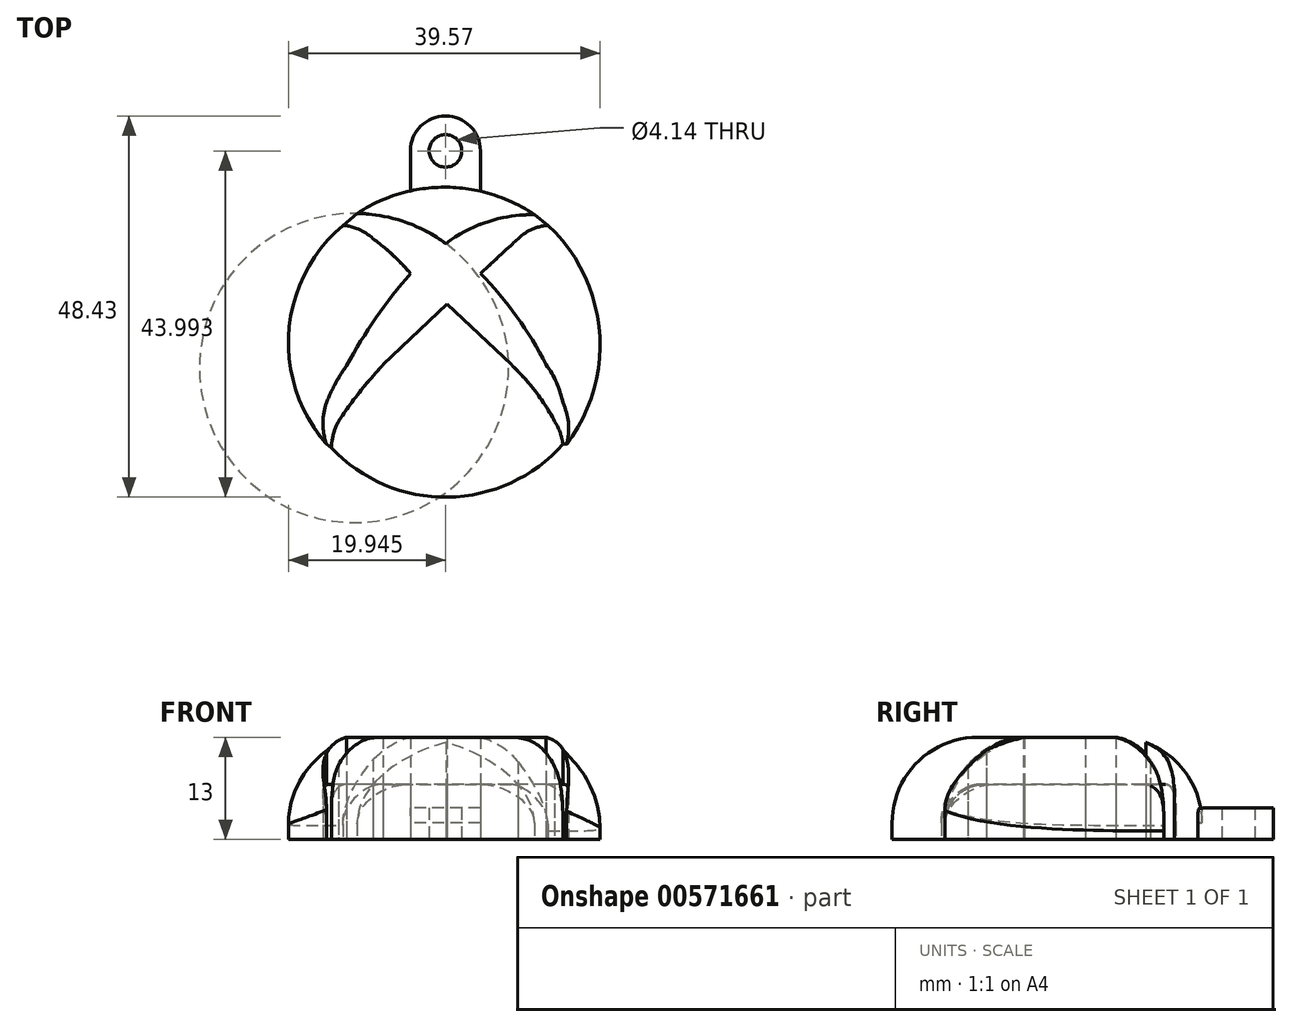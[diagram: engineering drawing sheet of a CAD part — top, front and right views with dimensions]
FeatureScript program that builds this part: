
annotation { "Feature Type Name" : "Feature", "Feature Type Description" : "" }
export const myFeature = defineFeature(function(context is Context, id is Id, definition is map)
    precondition{}
    {
        {
            var Q0;
            Q0=qCreatedBy(makeId("Top.planeOp"),FACE);
            var sketch = newSketch(context, id + "F0", { "sketchPlane" : qUnion([Q0])});
            skArc(sketch, "E0", {"start": v(-15.66, -12.74) * mm, "mid": v(-0.85, -19.01) * mm, "end": v(13.75, -12.28) * mm});
            skArc(sketch, "E1", {"start": v(-14.77, -9.37) * mm, "mid": v(-15.4, -11) * mm, "end": v(-15.66, -12.74) * mm});
            skArc(sketch, "E2", {"start": v(-9.08, -2.19) * mm, "mid": v(-12.07, -5.66) * mm, "end": v(-14.77, -9.37) * mm});
            skLineSegment(sketch, "E3", {"start": v(-9.08, -2.19) * mm, "end": v(-1, 5.53) * mm});
            skLineSegment(sketch, "E4", {"start": v(-1, 5.53) * mm, "end": v(7.2, -2.19) * mm});
            skArc(sketch, "E5", {"start": v(13.75, -12.28) * mm, "mid": v(13.38, -10.77) * mm, "end": v(12.71, -9.37) * mm});
            skArc(sketch, "E6", {"start": v(12.71, -9.37) * mm, "mid": v(10.24, -5.56) * mm, "end": v(7.2, -2.19) * mm});
            skArc(sketch, "E7", {"start": v(-14.2, 15.52) * mm, "mid": v(-21.06, 2.05) * mm, "end": v(-16.28, -12.28) * mm});
            skArc(sketch, "E8", {"start": v(-10.34, 13.8) * mm, "mid": v(-12.13, 14.99) * mm, "end": v(-14.2, 15.52) * mm});
            skArc(sketch, "E9", {"start": v(-5.6, 9.4) * mm, "mid": v(-7.85, 11.74) * mm, "end": v(-10.34, 13.8) * mm});
            skArc(sketch, "E10", {"start": v(-16.28, -7) * mm, "mid": v(-16.74, -9.64) * mm, "end": v(-16.28, -12.28) * mm});
            skArc(sketch, "E11", {"start": v(-13.72, -2.3) * mm, "mid": v(-15.15, -4.57) * mm, "end": v(-16.28, -7) * mm});
            skArc(sketch, "E12", {"start": v(-5.6, 9.4) * mm, "mid": v(-10, 3.78) * mm, "end": v(-13.72, -2.3) * mm});
            skArc(sketch, "E13", {"start": v(10.13, 16.87) * mm, "mid": v(-1.1, 20.37) * mm, "end": v(-12.38, 17.04) * mm});
            skArc(sketch, "E14", {"start": v(-1.12, 13.21) * mm, "mid": v(-6.46, 16) * mm, "end": v(-12.38, 17.04) * mm});
            skArc(sketch, "E15", {"start": v(10.13, 16.87) * mm, "mid": v(4.2, 15.98) * mm, "end": v(-1.12, 13.21) * mm});
            skArc(sketch, "E16", {"start": v(14.24, -12.28) * mm, "mid": v(18.38, 2.07) * mm, "end": v(11.86, 15.52) * mm});
            skArc(sketch, "E17", {"start": v(14.24, -12.28) * mm, "mid": v(14.45, -9.6) * mm, "end": v(13.75, -7) * mm});
            skArc(sketch, "E18", {"start": v(13.75, -7) * mm, "mid": v(12.94, -4.48) * mm, "end": v(11.62, -2.19) * mm});
            skArc(sketch, "E19", {"start": v(11.62, -2.19) * mm, "mid": v(7.89, 3.92) * mm, "end": v(3.28, 9.4) * mm});
            skArc(sketch, "E20", {"start": v(8.04, 13.8) * mm, "mid": v(5.66, 11.6) * mm, "end": v(3.28, 9.4) * mm});
            skArc(sketch, "E21", {"start": v(11.86, 15.52) * mm, "mid": v(9.8, 15) * mm, "end": v(8.04, 13.8) * mm});
            skLineSegment(sketch, "E22", {"start": v(-12.38, 17.04) * mm, "end": v(-14.2, 15.52) * mm});
            skLineSegment(sketch, "E23", {"start": v(10.13, 16.87) * mm, "end": v(11.86, 15.52) * mm});
            skLineSegment(sketch, "E24", {"start": v(14.24, -12.28) * mm, "end": v(13.75, -12.28) * mm});
            skLineSegment(sketch, "E25", {"start": v(-15.66, -12.74) * mm, "end": v(-16.28, -12.28) * mm});
            skLineSegment(sketch, "E26", {"start": v(-5.6, 19.9) * mm, "end": v(-5.6, 24.98) * mm});
            skLineSegment(sketch, "E27", {"start": v(3.28, 19.86) * mm, "end": v(3.28, 24.98) * mm});
            skArc(sketch, "E28", {"start": v(3.28, 24.98) * mm, "mid": v(-1.16, 29.42) * mm, "end": v(-5.6, 24.98) * mm});
            skCircle(sketch, "E29", {"center": v(-1.16, 24.98) * mm, "radius": 2.07 * mm});
            skSolve(sketch);
        }
        {
            var Q0;
            Q0=makeQuery(id+"F0.imprint","IMPRINT",FACE,{"disambiguationData":[TD([[makeQuery(id+"F0.imprint","IMPRINT",EDGE,{"derivedFrom":sQuery(id+"F0.wireOp",EDGE,"E0")}),1.0]])]});
            var Q1;
            Q1=makeQuery(id+"F0.imprint","IMPRINT",FACE,{"disambiguationData":[TD([[makeQuery(id+"F0.imprint","IMPRINT",EDGE,{"derivedFrom":sQuery(id+"F0.wireOp",EDGE,"E7")}),1.0]])]});
            var Q2;
            Q2=makeQuery(id+"F0.imprint","IMPRINT",FACE,{"disambiguationData":[TD([[makeQuery(id+"F0.imprint","IMPRINT",EDGE,{"derivedFrom":sQuery(id+"F0.wireOp",EDGE,"E13")}),1.0]])]});
            var Q3;
            Q3=makeQuery(id+"F0.imprint","IMPRINT",FACE,{"disambiguationData":[TD([[makeQuery(id+"F0.imprint","IMPRINT",EDGE,{"derivedFrom":sQuery(id+"F0.wireOp",EDGE,"E16")}),1.0]])]});
            extrude(context, id + "F1", {"entities" : qUnion([Q0, Q1, Q2, Q3]), "depth" : 13 * mm, "offsetDistance" : 25 * mm});
        }
        {
            var Q0;
            Q0=makeQuery(id+"F1.opExtrude","CAP_EDGE",EDGE,{"disambiguationData":[OSD([sQuery(id+"F0.wireOp",EDGE,"E0")])],"isStart":false});
            fillet(context, id + "F2", {"entities" : qUnion([Q0]), "radius" : 10.9 * mm, "tangentPropagation" : true, "allowEdgeOverflow" : false});
        }
        {
            var Q0;
            Q0=makeQuery(id+"F1.opExtrude","CAP_EDGE",EDGE,{"disambiguationData":[OSD([sQuery(id+"F0.wireOp",EDGE,"E7")])],"isStart":false});
            fillet(context, id + "F3", {"entities" : qUnion([Q0]), "radius" : 11.2 * mm, "tangentPropagation" : true, "allowEdgeOverflow" : false});
        }
        {
            var Q0;
            Q0=makeQuery(id+"F1.opExtrude","CAP_EDGE",EDGE,{"disambiguationData":[OSD([sQuery(id+"F0.wireOp",EDGE,"E13")])],"isStart":false});
            fillet(context, id + "F4", {"entities" : qUnion([Q0]), "radius" : 10.9 * mm, "tangentPropagation" : true, "allowEdgeOverflow" : false});
        }
        {
            var Q0;
            Q0=makeQuery(id+"F1.opExtrude","CAP_EDGE",EDGE,{"disambiguationData":[OSD([sQuery(id+"F0.wireOp",EDGE,"E16")])],"isStart":false});
            fillet(context, id + "F5", {"entities" : qUnion([Q0]), "radius" : 12 * mm, "tangentPropagation" : true, "allowEdgeOverflow" : false});
        }
        {
            var Q0;
            Q0=makeQuery(id+"F0.imprint","IMPRINT",FACE,{"disambiguationData":[TD([[makeQuery(id+"F0.imprint","IMPRINT",EDGE,{"derivedFrom":sQuery(id+"F0.wireOp",EDGE,"E1")}),-1.0]])]});
            extrude(context, id + "F6", {"entities" : qUnion([Q0]), "depth" : 7 * mm, "offsetDistance" : 25 * mm});
        }
        {
            var Q0;
            Q0=makeQuery(id+"F6.opExtrude","CAP_EDGE",EDGE,{"disambiguationData":[OSD([sQuery(id+"F0.wireOp",EDGE,"E25")])],"isStart":false});
            var Q1;
            Q1=makeQuery(id+"F6.opExtrude","CAP_EDGE",EDGE,{"disambiguationData":[OSD([sQuery(id+"F0.wireOp",EDGE,"E22")])],"isStart":false});
            var Q2;
            Q2=makeQuery(id+"F6.opExtrude","CAP_EDGE",EDGE,{"disambiguationData":[OSD([sQuery(id+"F0.wireOp",EDGE,"E23")])],"isStart":false});
            var Q3;
            Q3=makeQuery(id+"F6.opExtrude","CAP_EDGE",EDGE,{"disambiguationData":[OSD([sQuery(id+"F0.wireOp",EDGE,"E24")])],"isStart":false});
            fillet(context, id + "F7", {"entities" : qUnion([Q0, Q1, Q2, Q3]), "radius" : 5 * mm, "tangentPropagation" : true, "allowEdgeOverflow" : false});
        }
        {
            var Q0;
            {var subQ0=sQuery(id+"F0.wireOp",EDGE,"E26");Q0=makeQuery(id+"F0.imprint","IMPRINT",FACE,{"disambiguationData":[TD([[makeQuery(id+"F0.imprint","IMPRINT",EDGE,{"derivedFrom":subQ0}),-1.0]])]});}
            extrude(context, id + "F8", {"entities" : qUnion([Q0]), "operationType" : NewBodyOperationType.ADD, "depth" : 4 * mm, "offsetDistance" : 25 * mm});
        }
        {
            var Q0;
            Q0=makeQuery(id+"F8.opExtrude","CAP_EDGE",EDGE,{"disambiguationData":[OSD([sQuery(id+"F0.wireOp",EDGE,"E13")])],"isStart":false});
            fillet(context, id + "F9", {"entities" : qUnion([Q0]), "radius" : 1 * mm, "tangentPropagation" : true, "rho" : .8, "crossSection" : FilletCrossSection.CONIC, "allowEdgeOverflow" : false});
        }
    });
